# Revit family: Faucet_Kitchen-DXV-Victorian-D35402250_Series
name_source: partatom
category: Plumbing Fixtures
units: mm (PartAtom-declared; Revit-internal decimal feet)

## family parameters
Always vertical = No
Cut with Voids When Loaded = No
OmniClass Number = 23.45.55.17
OmniClass Title = Mixing Faucets
Part Type = Normal
Room Calculation Point = No
Round Connector Dimension = Use Diameter
Shared = Yes
Work Plane-Based = Yes

## types (3) — shared parameters
Assembly Code = D2020300
CW Connection = Yes
CWFU = 1.5
CalGreen Compliant = Yes
Cold Water Connection Diameter = 1/2"
Default Elevation = 0"
Description = VICTORIAN BRIDGE KITCHEN FAUCET
Flow Rate = 1.8 gpm (6.8 L/min)
HW Connection = Yes
HWFU = 1.5
Height = 12"
Hot Water Connection Diameter = 1"
IAPMO Compliance = Meets or Exceeds ASME A112.18.1/ CSA B125.1/NSF 61/Section 9
Installation Type = Deck Mounted
Length = 8 7/8"
Manufacturer = DXV
Price = Prices may vary. Please consult Manufacturer Representative for most up-to-date price list.
Product Documentation Link = https://dxv01.blob.core.windows.net
Product Page URL = https://www.dxv.com
Side Spray Connection Description = 3/8'' Supply Inlet
Side Spray Diameter = 3/8"
Side Spray Option = Yes
Side Spray Radius = 3/16"
Tempered Water Connection = Yes
Tempered Water Connection Diameter = 1/2"
URL = http://www.dxv.com
Vent Connection = No
WFU = 2
Warranty Documentation Link = https://www.dxv.com
Waste Connection = No
Width = 4 3/8"

## per-type parameters (varying)
| type | Finish | Material |
| D35402250.110 | Brass-DXV-110-Carbon Bronze | Brass-DXV-110-Carbon Bronze |
| D35402250.100 | Brass-DXV-100-Polished Chrome | Brass-DXV-100-Polished Chrome |
| D35402250.355 | Brass-DXV-355-Ultra Steel | Brass-DXV-355-Ultra Steel |

note: column(s) folded — value = type name in every type: Model

## geometry (parser evidence)
native form markers: Sweep x2
no freeform markers — native parametric forms only
